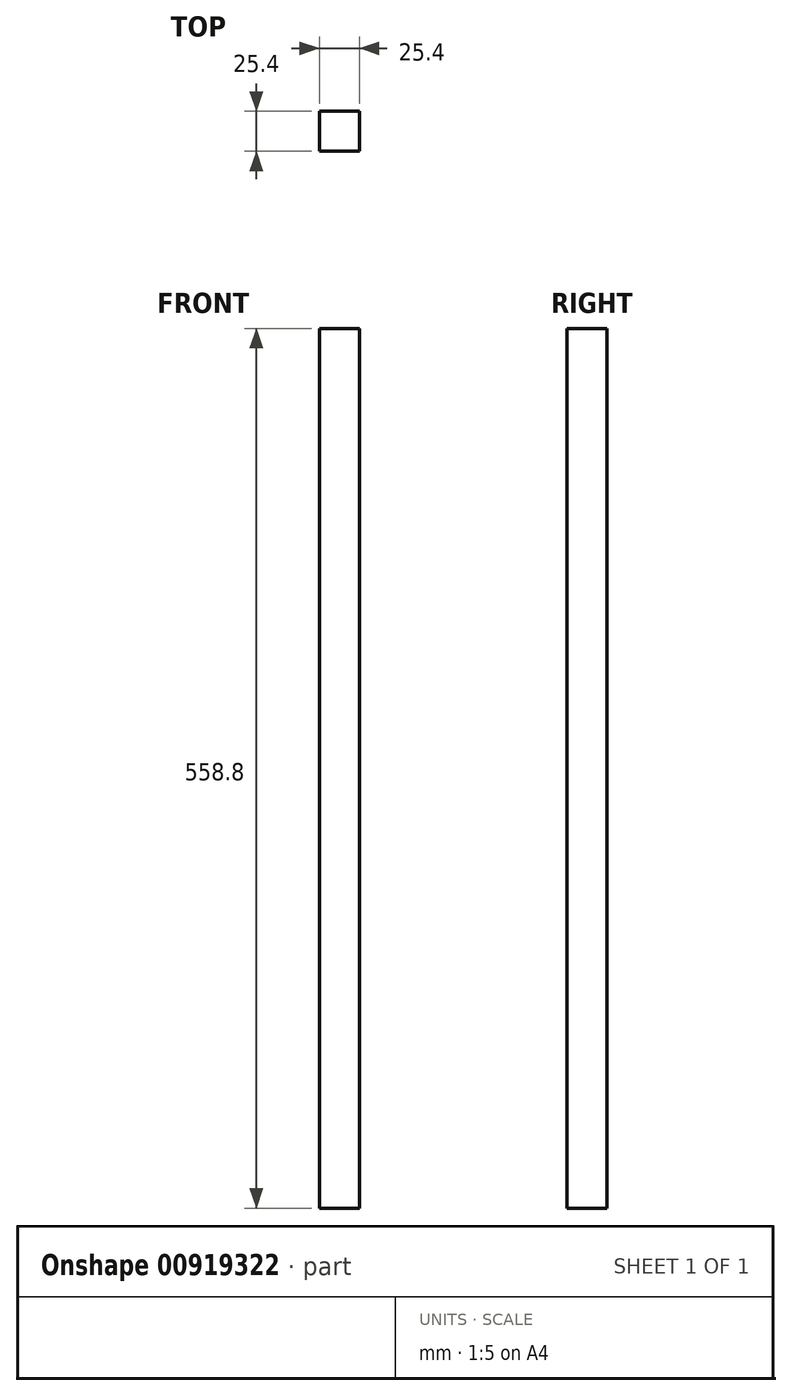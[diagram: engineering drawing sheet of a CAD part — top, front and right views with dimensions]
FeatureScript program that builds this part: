
annotation { "Feature Type Name" : "Feature", "Feature Type Description" : "" }
export const myFeature = defineFeature(function(context is Context, id is Id, definition is map)
    precondition{}
    {
        {
            var Q0;
            Q0=qCreatedBy(makeId("Top.planeOp"),FACE);
            var sketch = newSketch(context, id + "F0", { "sketchPlane" : qUnion([Q0])});
            skLineSegment(sketch, "E0.bottom", {"start": v(12.7, -12.7) * mm, "end": v(-12.7, -12.7) * mm});
            skLineSegment(sketch, "E0.top", {"start": v(12.7, 12.7) * mm, "end": v(-12.7, 12.7) * mm});
            skLineSegment(sketch, "E0.left", {"start": v(12.7, -12.7) * mm, "end": v(12.7, 12.7) * mm});
            skLineSegment(sketch, "E0.right", {"start": v(-12.7, -12.7) * mm, "end": v(-12.7, 12.7) * mm});
            skPoint(sketch, "E0.middle", {"position": v(0, 0) * mm});
            skSolve(sketch);
        }
        {
            var Q0;
            Q0=makeQuery(id+"F0.imprint","IMPRINT",FACE,{"disambiguationData":[TD([[makeQuery(id+"F0.imprint","IMPRINT",EDGE,{"derivedFrom":sQuery(id+"F0.wireOp",EDGE,"E0.bottom")}),-1.0]])]});
            var Q1;
            Q1 = qSketchRegion(id + "F0", true);
            extrude(context, id + "F1", {"entities" : qUnion([Q0, Q1]), "depth" : 558.8 * mm, "offsetDistance" : 25.4 * mm});
        }
    });
